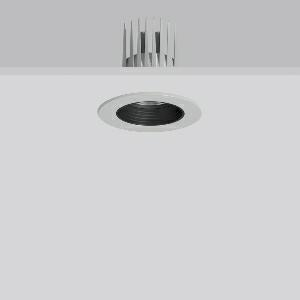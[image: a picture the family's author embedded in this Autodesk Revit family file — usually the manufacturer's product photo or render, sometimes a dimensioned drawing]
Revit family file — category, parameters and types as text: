
# Revit family: heledon_mini_e_901751_004_1_76_e551
name_source: partatom
category: Lighting Fixtures
units: mm (PartAtom-declared; Revit-internal decimal feet)

## family parameters
Cut with Voids When Loaded = No
Host = Face
Light Source = No
Part Type = Normal
Room Calculation Point = No
Round Connector Dimension = Use Diameter
Shared = No

## types (1)
- HELEDON mini E (1 x LED Modul 940, 3400 lm, 4000)
    Apparent Load = 29 VA
    Approval mark = CE
    CIE Flux Codes = 99 100 100 100 100
    Color Rendering = 92
    Color Temperature = 4000
    Default Elevation = 1800 mm
    Description = Series: HELEDON mini
Round recessed downlight. Housing: die-cast aluminium, powder-coated. Black plastic ring and recessed LED to prevent glare from the side. Optical assembly with lens made of plastic (polycarbonate) for the best homogeneous light distribution - can be changed without tools. Best colour rendering index Ra>90. Suitable for Recessed ceiling mounting. Installation without tools thanks to spring fastening system. Including separate LED converter with connecting cable 600 mm.High quality converter without flickering and stroboscopic effect. Through-wiring box (5 pole) available as accessory. The following accessories can be mounted without use of tools: interchangeable lenses, decorative glasses, honeycomb louvre, clear and frosted diffusers, white interchangeable plastic ring. 
Colour: silver
Diameter: 124 mm
Height: 3 mm
Cut-out diameter: 114 mm
Recess height: 170 mm
Luminaire: recess height: 120 mm
Lamp: LED
Socket: without socket
Colour temperature: 4000K
Colour rendering index (CRI): 92
System power: 29 W
Rated luminous flux: 3400 lm
Luminous efficiency: 117 lm/W
Control gear: Converter, dimmable, DALI
Protection class: II
Type of protection: IP 20
    Height = 0 mm  [stored 0 ft]
    Lamp = 1 x LED Modul 940
    Lamp Light Flux = 3400 lm
    Lamp count = 1
    Length = 124 mm  [stored 0.406824 ft]
    Lifetime = 50000 h
    Luminous efficacy = 117 lm/W
    Manufacturer = RZB
    ModVariant = No
    Model = 901751.004.1.76
    Mounting Place = Ceiling
    Mounting Type = Recessed
    Number of Poles = 1
    OnlyDefault = Yes
    Power Factor = 1
    Product Name = HELEDON mini E
    Product group = Recessed downlights
    ProductGroupID = 402
    Protection Class = Protection class II
    Protection Degree = IP 20
    RLX_Detail_Level = 1
    RLX_Emergency_Light_Flux = 0 lm
    RLX_Emergency_Type = 0
    RLX_Emergency_Type_DB = No
    RlxData = <blob elided: 126141 chars, md5=015dae50>
    Socket = socket
    Standby Power = 0 W
    System Light Flux = 3400 lm
    System Power = 29 W
    Type Comments = Product without accessories
    Type Image = 901656.004.jpg
    URL = http://relux.com
    VarID = ---
    Voltage = 230 V
    Voltage Range = 220-240 V
    Weight = 0.00 kg
    Width = 0 mm  [stored 0 ft]

note: [stored X ft] marks values corroborated as IEEE doubles in the binary element streams (Revit-internal decimal feet)

## geometry (parser evidence)
native form markers: Blend x4, Sweep x12
no freeform markers — native parametric forms only
